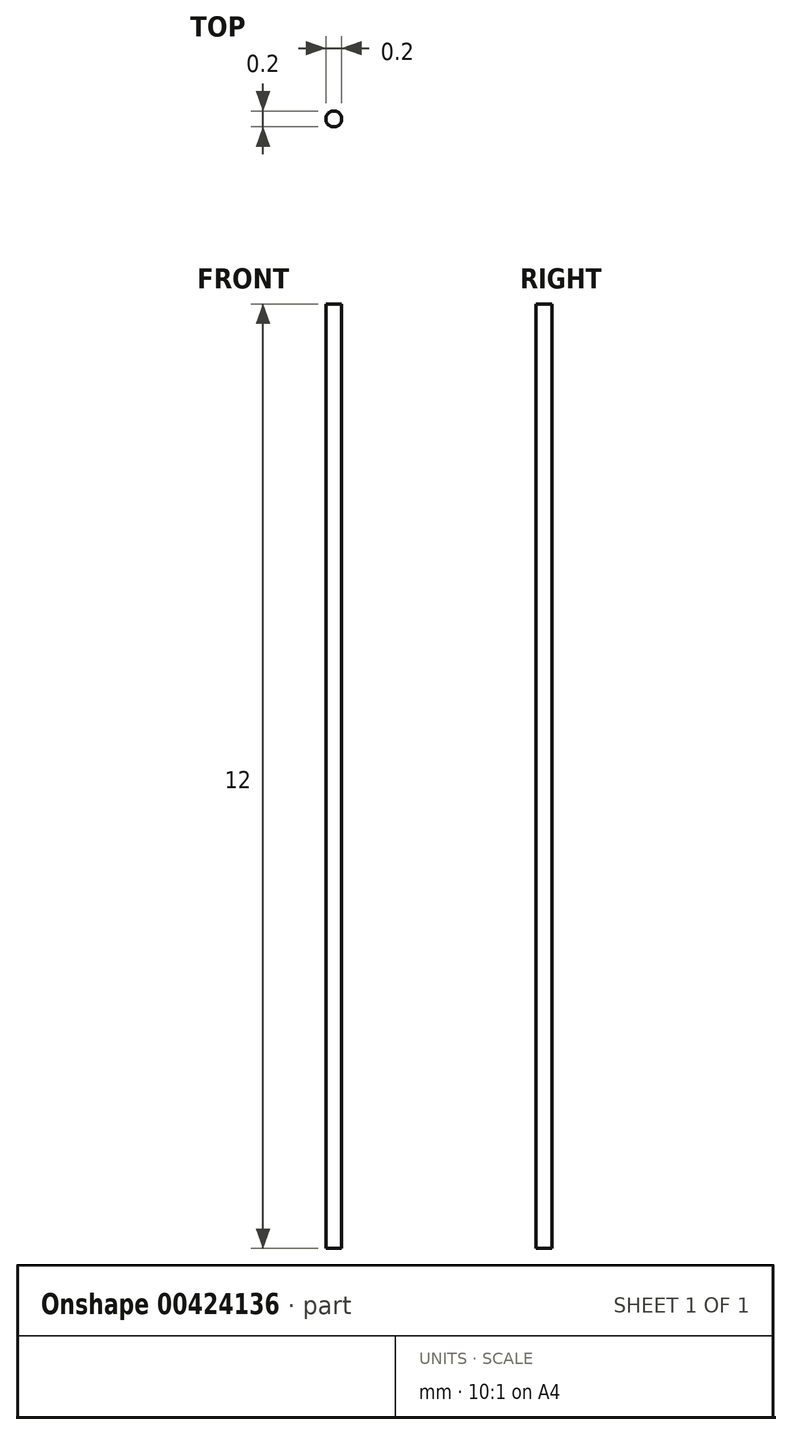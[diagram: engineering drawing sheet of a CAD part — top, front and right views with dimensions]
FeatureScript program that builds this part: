
annotation { "Feature Type Name" : "Feature", "Feature Type Description" : "" }
export const myFeature = defineFeature(function(context is Context, id is Id, definition is map)
    precondition{}
    {
        {
            var Q0;
            Q0=qCreatedBy(makeId("Top.planeOp"),FACE);
            var sketch = newSketch(context, id + "F0", { "sketchPlane" : qUnion([Q0])});
            skCircle(sketch, "E0", {"center": v(0, 0) * mm, "radius": 0.1 * mm});
            skSolve(sketch);
        }
        {
            var Q0;
            Q0 = qSketchRegion(id + "F0", true);
            extrude(context, id + "F1", {"entities" : qUnion([Q0]), "depth" : 12 * mm});
        }
    });
